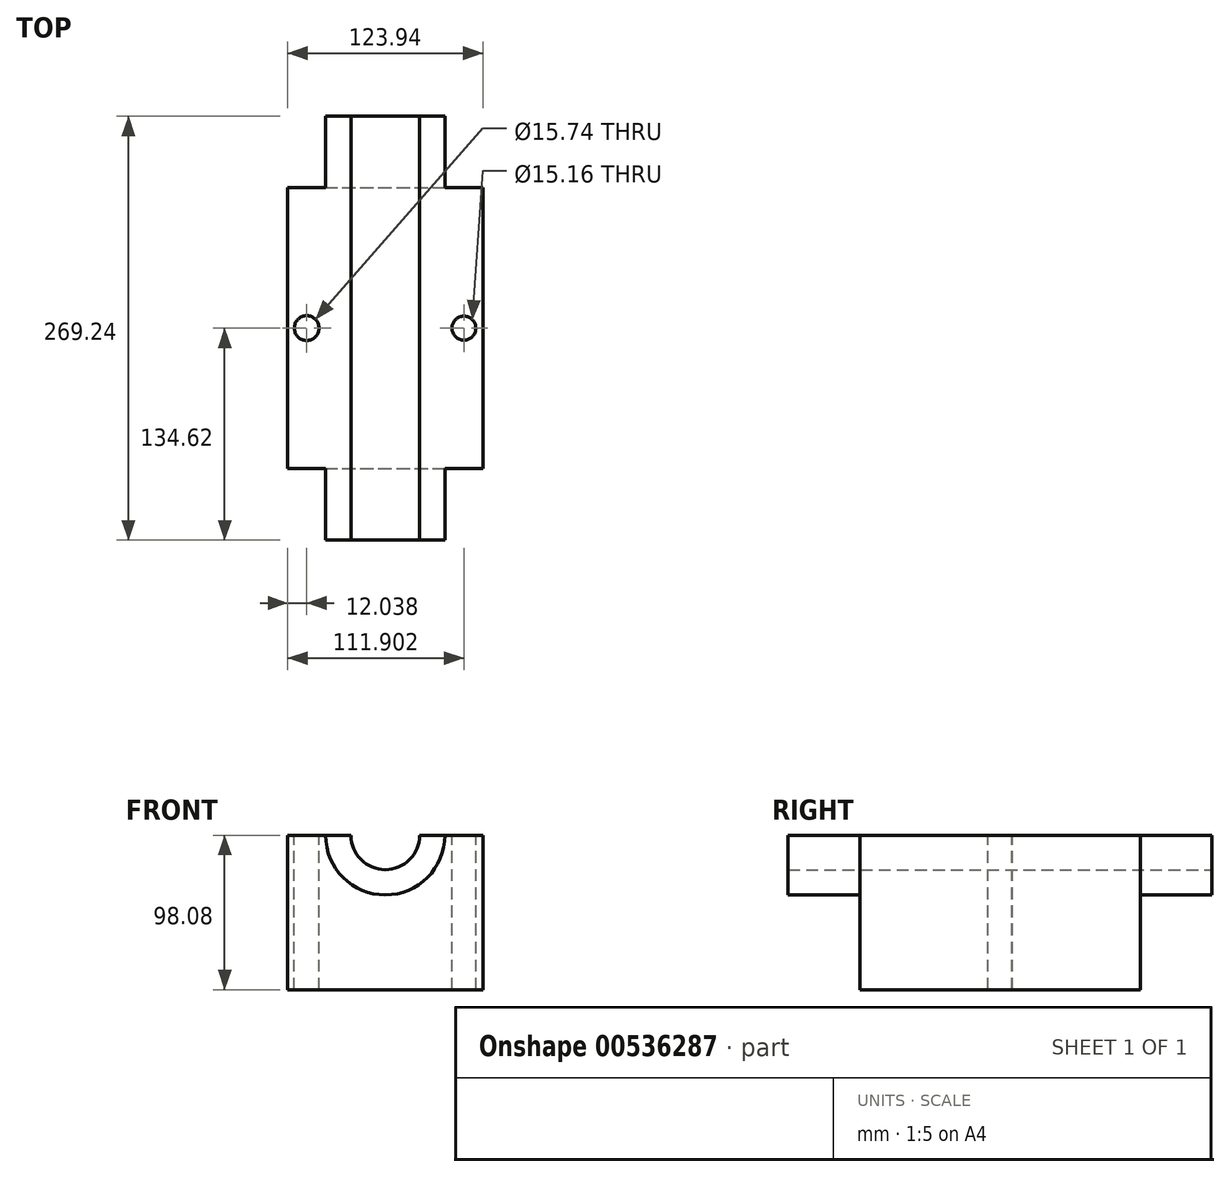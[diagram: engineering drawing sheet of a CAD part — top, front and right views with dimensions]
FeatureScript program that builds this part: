
annotation { "Feature Type Name" : "Feature", "Feature Type Description" : "" }
export const myFeature = defineFeature(function(context is Context, id is Id, definition is map)
    precondition{}
    {
        {
            var Q0;
            Q0=qCreatedBy(makeId("Front.planeOp"),FACE);
            var sketch = newSketch(context, id + "F0", { "sketchPlane" : qUnion([Q0])});
            skLineSegment(sketch, "E0.bottom", {"start": v(-61.97, 49.04) * mm, "end": v(-21.85, 49.04) * mm});
            skLineSegment(sketch, "E0.top", {"start": v(-61.97, -49.04) * mm, "end": v(61.97, -49.04) * mm});
            skLineSegment(sketch, "E0.left", {"start": v(-61.97, 49.04) * mm, "end": v(-61.97, -49.04) * mm});
            skLineSegment(sketch, "E0.right", {"start": v(61.97, 49.04) * mm, "end": v(61.97, -49.04) * mm});
            skPoint(sketch, "E0.middle", {"position": v(0, 0) * mm});
            skArc(sketch, "E1", {"start": v(-37.9, 49.04) * mm, "mid": v(0, 11.15) * mm, "end": v(37.9, 49.04) * mm});
            skArc(sketch, "E2", {"start": v(-21.85, 49.04) * mm, "mid": v(0, 27.2) * mm, "end": v(21.85, 49.04) * mm});
            skLineSegment(sketch, "E3.trimOffspring", {"start": v(21.85, 49.04) * mm, "end": v(61.97, 49.04) * mm});
            skSolve(sketch);
        }
        {
            var Q0;
            {var subQ2=sQuery(id+"F0.wireOp",EDGE,"E1");Q0=makeQuery(id+"F0.imprint","IMPRINT",FACE,{"disambiguationData":[TD([[makeQuery(id+"F0.imprint","IMPRINT",EDGE,{"derivedFrom":subQ2}),1.0]])]});}
            extrude(context, id + "F1", {"entities" : qUnion([Q0]), "endBound" : BoundingType.SYMMETRIC, "depth" : 269.24 * mm, "offsetDistance" : 25.4 * mm});
        }
        {
            var Q0;
            Q0=makeQuery(id+"F0.imprint","IMPRINT",FACE,{"disambiguationData":[TD([[makeQuery(id+"F0.imprint","IMPRINT",EDGE,{"derivedFrom":sQuery(id+"F0.wireOp",EDGE,"E0.top")}),1.0]])]});
            extrude(context, id + "F2", {"entities" : qUnion([Q0]), "operationType" : NewBodyOperationType.ADD, "endBound" : BoundingType.SYMMETRIC, "depth" : 178.3 * mm, "offsetDistance" : 25.4 * mm});
        }
        {
            var Q0;
            {var subQ0=sQuery(id+"F0.wireOp",EDGE,"E0.bottom");Q0=makeQuery(id+"F2.boolean.opBoolean","MERGE",FACE,{"derivedFrom":[makeQuery(id+"F1.opExtrude","SWEPT_FACE",FACE,{"disambiguationData":[OSD([subQ0])]}),makeQuery(id+"F2.opExtrude","SWEPT_FACE",FACE,{"disambiguationData":[OSD([subQ0])]})]});}
            var sketch = newSketch(context, id + "F3", { "sketchPlane" : qUnion([Q0])});
            skCircle(sketch, "E4", {"center": v(-49.93, 0) * mm, "radius": 7.87 * mm});
            skPoint(sketch, "E4.centerSnap0", {"position": v(-49.93, 89.15) * mm});
            skPoint(sketch, "E4.centerSnap1", {"position": v(-61.97, 0) * mm});
            skSolve(sketch);
        }
        {
            var Q0;
            {var subQ0=sQuery(id+"F0.wireOp",EDGE,"E3.trimOffspring");Q0=makeQuery(id+"F2.boolean.opBoolean","MERGE",FACE,{"derivedFrom":[makeQuery(id+"F1.opExtrude","SWEPT_FACE",FACE,{"disambiguationData":[OSD([subQ0])]}),makeQuery(id+"F2.opExtrude","SWEPT_FACE",FACE,{"disambiguationData":[OSD([subQ0])]})]});}
            var sketch = newSketch(context, id + "F4", { "sketchPlane" : qUnion([Q0])});
            skCircle(sketch, "E5", {"center": v(49.93, 0) * mm, "radius": 7.58 * mm});
            skPoint(sketch, "E5.centerSnap0", {"position": v(49.93, 89.15) * mm});
            skPoint(sketch, "E5.centerSnap1", {"position": v(61.97, 0) * mm});
            skSolve(sketch);
        }
        {
            var Q0;
            Q0=makeQuery(id+"F3.imprint","IMPRINT",FACE,{"disambiguationData":[TD([[makeQuery(id+"F3.imprint","IMPRINT",EDGE,{"derivedFrom":sQuery(id+"F3.wireOp",EDGE,"E4")}),1.0]])]});
            var Q1;
            Q1=sQuery(id+"F3.wireOp",EDGE,"E4");
            extrude(context, id + "F5", {"entities" : qUnion([Q0]), "operationType" : NewBodyOperationType.REMOVE, "surfaceEntities" : qUnion([Q1]), "oppositeDirection" : true, "depth" : 98.08 * mm, "offsetDistance" : 25.4 * mm});
        }
        {
            var Q0;
            Q0=makeQuery(id+"F4.imprint","IMPRINT",FACE,{"disambiguationData":[TD([[makeQuery(id+"F4.imprint","IMPRINT",EDGE,{"derivedFrom":sQuery(id+"F4.wireOp",EDGE,"E5")}),1.0]])]});
            var Q1;
            Q1=sQuery(id+"F4.wireOp",EDGE,"E5");
            extrude(context, id + "F6", {"entities" : qUnion([Q0]), "operationType" : NewBodyOperationType.REMOVE, "surfaceEntities" : qUnion([Q1]), "oppositeDirection" : true, "depth" : 98.08 * mm, "offsetDistance" : 25.4 * mm});
        }
    });
